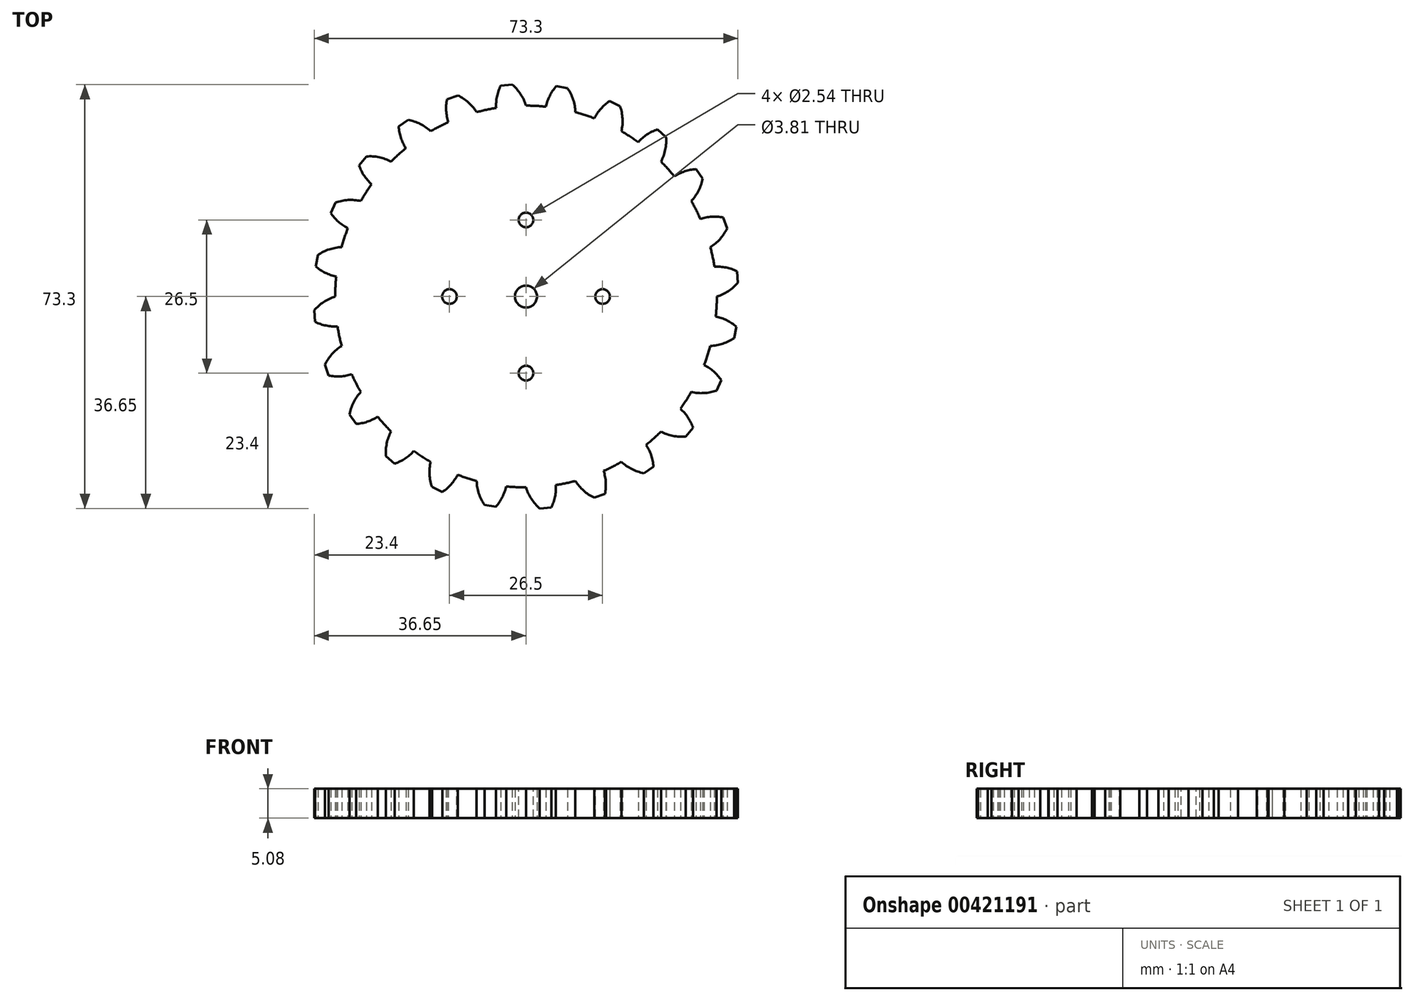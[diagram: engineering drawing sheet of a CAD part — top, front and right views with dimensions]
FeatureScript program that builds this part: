
annotation { "Feature Type Name" : "Feature", "Feature Type Description" : "" }
export const myFeature = defineFeature(function(context is Context, id is Id, definition is map)
    precondition{}
    {
        {
            var Q0;
            Q0=qCreatedBy(makeId("Top.planeOp"),FACE);
            var sketch = newSketch(context, id + "F0", { "sketchPlane" : qUnion([Q0])});
            skCircle(sketch, "E0", {"center": v(-444.5, 30.48) * mm, "radius": 1.9 * mm});
            skArc(sketch, "E1", {"start": v(-411.89, 35.65) * mm, "mid": v(-477.42, 27.89) * mm, "end": v(-411.48, 30.48) * mm});
            skArc(sketch, "E2", {"start": v(-408, 34.85) * mm, "mid": v(-409.9, 35.5) * mm, "end": v(-411.89, 35.65) * mm});
            skArc(sketch, "E3", {"start": v(-411.48, 30.48) * mm, "mid": v(-409.5, 31.41) * mm, "end": v(-407.85, 32.86) * mm});
            skLineSegment(sketch, "E4", {"start": v(-407.85, 32.86) * mm, "end": v(-408, 34.85) * mm});
            skSolve(sketch);
        }
        {
            var Q0;
            Q0=makeQuery(id+"F0.imprint","IMPRINT",FACE,{"disambiguationData":[TD([[makeQuery(id+"F0.imprint","IMPRINT",EDGE,{"derivedFrom":sQuery(id+"F0.wireOp",EDGE,"E0")}),-1.0]])]});
            extrude(context, id + "F1", {"entities" : qUnion([Q0]), "depth" : 5.08 * mm});
        }
        {
            var Q0;
            Q0=makeQuery(id+"F1.opExtrude","SWEPT_BODY",BODY,{"disambiguationData":[OSD([sQuery(id+"F0.wireOp",EDGE,"E0"),sQuery(id+"F0.wireOp",EDGE,"mfvC6Oh1-3P4Q-e3RM-1CXu-yx0pQRPToK0Y"),sQuery(id+"F0.wireOp",EDGE,"9eBLdcwT-yV5s-1o6b-eXcZ-bTUMROUA1rMA"),sQuery(id+"F0.wireOp",EDGE,"zkpdbw0p-lr3g-EBgj-NubB-pjmDa1DJFhjj"),sQuery(id+"F0.wireOp",EDGE,"jBF4Mbbw-OiBo-sLmE-1t8X-jgWY8rPl5u1C")])]});
            var Q1;
            Q1=makeQuery(id+"F1.opExtrude","SWEPT_FACE",FACE,{"disambiguationData":[OSD([sQuery(id+"F0.wireOp",EDGE,"E1")])]});
            circularPattern(context, id + "F2", {"entities" : qUnion([Q0]), "axis" : qUnion([Q1]), "angle" : 360 * degree, "instanceCount" : 24, "equalSpace" : true});
        }
        {
            var Q0;
            Q0=makeQuery(id+"F1.opExtrude","SWEPT_BODY",BODY,{"disambiguationData":[OSD([sQuery(id+"F0.wireOp",EDGE,"E0"),sQuery(id+"F0.wireOp",EDGE,"9eBLdcwT-yV5s-1o6b-eXcZ-bTUMROUA1rMA"),sQuery(id+"F0.wireOp",EDGE,"zkpdbw0p-lr3g-EBgj-NubB-pjmDa1DJFhjj"),sQuery(id+"F0.wireOp",EDGE,"jBF4Mbbw-OiBo-sLmE-1t8X-jgWY8rPl5u1C"),sQuery(id+"F0.wireOp",EDGE,"E1")])]});
            var Q1;
            Q1=makeQuery(id+"F2.opPattern","COPY",BODY,{"derivedFrom":makeQuery(id+"F1.opExtrude","SWEPT_BODY",BODY,{"disambiguationData":[OSD([sQuery(id+"F0.wireOp",EDGE,"E0"),sQuery(id+"F0.wireOp",EDGE,"9eBLdcwT-yV5s-1o6b-eXcZ-bTUMROUA1rMA"),sQuery(id+"F0.wireOp",EDGE,"zkpdbw0p-lr3g-EBgj-NubB-pjmDa1DJFhjj"),sQuery(id+"F0.wireOp",EDGE,"jBF4Mbbw-OiBo-sLmE-1t8X-jgWY8rPl5u1C"),sQuery(id+"F0.wireOp",EDGE,"E1")])]}),"instanceName":"1"});
            var Q2;
            Q2=makeQuery(id+"F2.opPattern","COPY",BODY,{"derivedFrom":makeQuery(id+"F1.opExtrude","SWEPT_BODY",BODY,{"disambiguationData":[OSD([sQuery(id+"F0.wireOp",EDGE,"E0"),sQuery(id+"F0.wireOp",EDGE,"9eBLdcwT-yV5s-1o6b-eXcZ-bTUMROUA1rMA"),sQuery(id+"F0.wireOp",EDGE,"zkpdbw0p-lr3g-EBgj-NubB-pjmDa1DJFhjj"),sQuery(id+"F0.wireOp",EDGE,"jBF4Mbbw-OiBo-sLmE-1t8X-jgWY8rPl5u1C"),sQuery(id+"F0.wireOp",EDGE,"E1")])]}),"instanceName":"2"});
            var Q3;
            Q3=makeQuery(id+"F2.opPattern","COPY",BODY,{"derivedFrom":makeQuery(id+"F1.opExtrude","SWEPT_BODY",BODY,{"disambiguationData":[OSD([sQuery(id+"F0.wireOp",EDGE,"E0"),sQuery(id+"F0.wireOp",EDGE,"9eBLdcwT-yV5s-1o6b-eXcZ-bTUMROUA1rMA"),sQuery(id+"F0.wireOp",EDGE,"zkpdbw0p-lr3g-EBgj-NubB-pjmDa1DJFhjj"),sQuery(id+"F0.wireOp",EDGE,"jBF4Mbbw-OiBo-sLmE-1t8X-jgWY8rPl5u1C"),sQuery(id+"F0.wireOp",EDGE,"E1")])]}),"instanceName":"3"});
            var Q4;
            Q4=makeQuery(id+"F2.opPattern","COPY",BODY,{"derivedFrom":makeQuery(id+"F1.opExtrude","SWEPT_BODY",BODY,{"disambiguationData":[OSD([sQuery(id+"F0.wireOp",EDGE,"E0"),sQuery(id+"F0.wireOp",EDGE,"9eBLdcwT-yV5s-1o6b-eXcZ-bTUMROUA1rMA"),sQuery(id+"F0.wireOp",EDGE,"zkpdbw0p-lr3g-EBgj-NubB-pjmDa1DJFhjj"),sQuery(id+"F0.wireOp",EDGE,"jBF4Mbbw-OiBo-sLmE-1t8X-jgWY8rPl5u1C"),sQuery(id+"F0.wireOp",EDGE,"E1")])]}),"instanceName":"4"});
            var Q5;
            Q5=makeQuery(id+"F2.opPattern","COPY",BODY,{"derivedFrom":makeQuery(id+"F1.opExtrude","SWEPT_BODY",BODY,{"disambiguationData":[OSD([sQuery(id+"F0.wireOp",EDGE,"E0"),sQuery(id+"F0.wireOp",EDGE,"9eBLdcwT-yV5s-1o6b-eXcZ-bTUMROUA1rMA"),sQuery(id+"F0.wireOp",EDGE,"zkpdbw0p-lr3g-EBgj-NubB-pjmDa1DJFhjj"),sQuery(id+"F0.wireOp",EDGE,"jBF4Mbbw-OiBo-sLmE-1t8X-jgWY8rPl5u1C"),sQuery(id+"F0.wireOp",EDGE,"E1")])]}),"instanceName":"5"});
            var Q6;
            Q6=makeQuery(id+"F2.opPattern","COPY",BODY,{"derivedFrom":makeQuery(id+"F1.opExtrude","SWEPT_BODY",BODY,{"disambiguationData":[OSD([sQuery(id+"F0.wireOp",EDGE,"E0"),sQuery(id+"F0.wireOp",EDGE,"9eBLdcwT-yV5s-1o6b-eXcZ-bTUMROUA1rMA"),sQuery(id+"F0.wireOp",EDGE,"zkpdbw0p-lr3g-EBgj-NubB-pjmDa1DJFhjj"),sQuery(id+"F0.wireOp",EDGE,"jBF4Mbbw-OiBo-sLmE-1t8X-jgWY8rPl5u1C"),sQuery(id+"F0.wireOp",EDGE,"E1")])]}),"instanceName":"6"});
            var Q7;
            Q7=makeQuery(id+"F2.opPattern","COPY",BODY,{"derivedFrom":makeQuery(id+"F1.opExtrude","SWEPT_BODY",BODY,{"disambiguationData":[OSD([sQuery(id+"F0.wireOp",EDGE,"E0"),sQuery(id+"F0.wireOp",EDGE,"9eBLdcwT-yV5s-1o6b-eXcZ-bTUMROUA1rMA"),sQuery(id+"F0.wireOp",EDGE,"zkpdbw0p-lr3g-EBgj-NubB-pjmDa1DJFhjj"),sQuery(id+"F0.wireOp",EDGE,"jBF4Mbbw-OiBo-sLmE-1t8X-jgWY8rPl5u1C"),sQuery(id+"F0.wireOp",EDGE,"E1")])]}),"instanceName":"11"});
            var Q8;
            Q8=makeQuery(id+"F2.opPattern","COPY",BODY,{"derivedFrom":makeQuery(id+"F1.opExtrude","SWEPT_BODY",BODY,{"disambiguationData":[OSD([sQuery(id+"F0.wireOp",EDGE,"E0"),sQuery(id+"F0.wireOp",EDGE,"9eBLdcwT-yV5s-1o6b-eXcZ-bTUMROUA1rMA"),sQuery(id+"F0.wireOp",EDGE,"zkpdbw0p-lr3g-EBgj-NubB-pjmDa1DJFhjj"),sQuery(id+"F0.wireOp",EDGE,"jBF4Mbbw-OiBo-sLmE-1t8X-jgWY8rPl5u1C"),sQuery(id+"F0.wireOp",EDGE,"E1")])]}),"instanceName":"14"});
            var Q9;
            Q9=makeQuery(id+"F2.opPattern","COPY",BODY,{"derivedFrom":makeQuery(id+"F1.opExtrude","SWEPT_BODY",BODY,{"disambiguationData":[OSD([sQuery(id+"F0.wireOp",EDGE,"E0"),sQuery(id+"F0.wireOp",EDGE,"9eBLdcwT-yV5s-1o6b-eXcZ-bTUMROUA1rMA"),sQuery(id+"F0.wireOp",EDGE,"zkpdbw0p-lr3g-EBgj-NubB-pjmDa1DJFhjj"),sQuery(id+"F0.wireOp",EDGE,"jBF4Mbbw-OiBo-sLmE-1t8X-jgWY8rPl5u1C"),sQuery(id+"F0.wireOp",EDGE,"E1")])]}),"instanceName":"12"});
            var Q10;
            Q10=makeQuery(id+"F2.opPattern","COPY",BODY,{"derivedFrom":makeQuery(id+"F1.opExtrude","SWEPT_BODY",BODY,{"disambiguationData":[OSD([sQuery(id+"F0.wireOp",EDGE,"E0"),sQuery(id+"F0.wireOp",EDGE,"9eBLdcwT-yV5s-1o6b-eXcZ-bTUMROUA1rMA"),sQuery(id+"F0.wireOp",EDGE,"zkpdbw0p-lr3g-EBgj-NubB-pjmDa1DJFhjj"),sQuery(id+"F0.wireOp",EDGE,"jBF4Mbbw-OiBo-sLmE-1t8X-jgWY8rPl5u1C"),sQuery(id+"F0.wireOp",EDGE,"E1")])]}),"instanceName":"13"});
            var Q11;
            Q11=makeQuery(id+"F2.opPattern","COPY",BODY,{"derivedFrom":makeQuery(id+"F1.opExtrude","SWEPT_BODY",BODY,{"disambiguationData":[OSD([sQuery(id+"F0.wireOp",EDGE,"E0"),sQuery(id+"F0.wireOp",EDGE,"9eBLdcwT-yV5s-1o6b-eXcZ-bTUMROUA1rMA"),sQuery(id+"F0.wireOp",EDGE,"zkpdbw0p-lr3g-EBgj-NubB-pjmDa1DJFhjj"),sQuery(id+"F0.wireOp",EDGE,"jBF4Mbbw-OiBo-sLmE-1t8X-jgWY8rPl5u1C"),sQuery(id+"F0.wireOp",EDGE,"E1")])]}),"instanceName":"19"});
            var Q12;
            Q12=makeQuery(id+"F2.opPattern","COPY",BODY,{"derivedFrom":makeQuery(id+"F1.opExtrude","SWEPT_BODY",BODY,{"disambiguationData":[OSD([sQuery(id+"F0.wireOp",EDGE,"E0"),sQuery(id+"F0.wireOp",EDGE,"9eBLdcwT-yV5s-1o6b-eXcZ-bTUMROUA1rMA"),sQuery(id+"F0.wireOp",EDGE,"zkpdbw0p-lr3g-EBgj-NubB-pjmDa1DJFhjj"),sQuery(id+"F0.wireOp",EDGE,"jBF4Mbbw-OiBo-sLmE-1t8X-jgWY8rPl5u1C"),sQuery(id+"F0.wireOp",EDGE,"E1")])]}),"instanceName":"18"});
            var Q13;
            Q13=makeQuery(id+"F2.opPattern","COPY",BODY,{"derivedFrom":makeQuery(id+"F1.opExtrude","SWEPT_BODY",BODY,{"disambiguationData":[OSD([sQuery(id+"F0.wireOp",EDGE,"E0"),sQuery(id+"F0.wireOp",EDGE,"9eBLdcwT-yV5s-1o6b-eXcZ-bTUMROUA1rMA"),sQuery(id+"F0.wireOp",EDGE,"zkpdbw0p-lr3g-EBgj-NubB-pjmDa1DJFhjj"),sQuery(id+"F0.wireOp",EDGE,"jBF4Mbbw-OiBo-sLmE-1t8X-jgWY8rPl5u1C"),sQuery(id+"F0.wireOp",EDGE,"E1")])]}),"instanceName":"17"});
            var Q14;
            Q14=makeQuery(id+"F2.opPattern","COPY",BODY,{"derivedFrom":makeQuery(id+"F1.opExtrude","SWEPT_BODY",BODY,{"disambiguationData":[OSD([sQuery(id+"F0.wireOp",EDGE,"E0"),sQuery(id+"F0.wireOp",EDGE,"9eBLdcwT-yV5s-1o6b-eXcZ-bTUMROUA1rMA"),sQuery(id+"F0.wireOp",EDGE,"zkpdbw0p-lr3g-EBgj-NubB-pjmDa1DJFhjj"),sQuery(id+"F0.wireOp",EDGE,"jBF4Mbbw-OiBo-sLmE-1t8X-jgWY8rPl5u1C"),sQuery(id+"F0.wireOp",EDGE,"E1")])]}),"instanceName":"10"});
            var Q15;
            Q15=makeQuery(id+"F2.opPattern","COPY",BODY,{"derivedFrom":makeQuery(id+"F1.opExtrude","SWEPT_BODY",BODY,{"disambiguationData":[OSD([sQuery(id+"F0.wireOp",EDGE,"E0"),sQuery(id+"F0.wireOp",EDGE,"9eBLdcwT-yV5s-1o6b-eXcZ-bTUMROUA1rMA"),sQuery(id+"F0.wireOp",EDGE,"zkpdbw0p-lr3g-EBgj-NubB-pjmDa1DJFhjj"),sQuery(id+"F0.wireOp",EDGE,"jBF4Mbbw-OiBo-sLmE-1t8X-jgWY8rPl5u1C"),sQuery(id+"F0.wireOp",EDGE,"E1")])]}),"instanceName":"16"});
            var Q16;
            Q16=makeQuery(id+"F2.opPattern","COPY",BODY,{"derivedFrom":makeQuery(id+"F1.opExtrude","SWEPT_BODY",BODY,{"disambiguationData":[OSD([sQuery(id+"F0.wireOp",EDGE,"E0"),sQuery(id+"F0.wireOp",EDGE,"9eBLdcwT-yV5s-1o6b-eXcZ-bTUMROUA1rMA"),sQuery(id+"F0.wireOp",EDGE,"zkpdbw0p-lr3g-EBgj-NubB-pjmDa1DJFhjj"),sQuery(id+"F0.wireOp",EDGE,"jBF4Mbbw-OiBo-sLmE-1t8X-jgWY8rPl5u1C"),sQuery(id+"F0.wireOp",EDGE,"E1")])]}),"instanceName":"15"});
            var Q17;
            Q17=makeQuery(id+"F2.opPattern","COPY",BODY,{"derivedFrom":makeQuery(id+"F1.opExtrude","SWEPT_BODY",BODY,{"disambiguationData":[OSD([sQuery(id+"F0.wireOp",EDGE,"E0"),sQuery(id+"F0.wireOp",EDGE,"9eBLdcwT-yV5s-1o6b-eXcZ-bTUMROUA1rMA"),sQuery(id+"F0.wireOp",EDGE,"zkpdbw0p-lr3g-EBgj-NubB-pjmDa1DJFhjj"),sQuery(id+"F0.wireOp",EDGE,"jBF4Mbbw-OiBo-sLmE-1t8X-jgWY8rPl5u1C"),sQuery(id+"F0.wireOp",EDGE,"E1")])]}),"instanceName":"9"});
            var Q18;
            Q18=makeQuery(id+"F2.opPattern","COPY",BODY,{"derivedFrom":makeQuery(id+"F1.opExtrude","SWEPT_BODY",BODY,{"disambiguationData":[OSD([sQuery(id+"F0.wireOp",EDGE,"E0"),sQuery(id+"F0.wireOp",EDGE,"9eBLdcwT-yV5s-1o6b-eXcZ-bTUMROUA1rMA"),sQuery(id+"F0.wireOp",EDGE,"zkpdbw0p-lr3g-EBgj-NubB-pjmDa1DJFhjj"),sQuery(id+"F0.wireOp",EDGE,"jBF4Mbbw-OiBo-sLmE-1t8X-jgWY8rPl5u1C"),sQuery(id+"F0.wireOp",EDGE,"E1")])]}),"instanceName":"8"});
            var Q19;
            Q19=makeQuery(id+"F2.opPattern","COPY",BODY,{"derivedFrom":makeQuery(id+"F1.opExtrude","SWEPT_BODY",BODY,{"disambiguationData":[OSD([sQuery(id+"F0.wireOp",EDGE,"E0"),sQuery(id+"F0.wireOp",EDGE,"9eBLdcwT-yV5s-1o6b-eXcZ-bTUMROUA1rMA"),sQuery(id+"F0.wireOp",EDGE,"zkpdbw0p-lr3g-EBgj-NubB-pjmDa1DJFhjj"),sQuery(id+"F0.wireOp",EDGE,"jBF4Mbbw-OiBo-sLmE-1t8X-jgWY8rPl5u1C"),sQuery(id+"F0.wireOp",EDGE,"E1")])]}),"instanceName":"7"});
            booleanBodies(context, id + "F3", {"operationType" : BooleanOperationType.UNION, "tools" : qUnion([Q0, Q1, Q2, Q3, Q4, Q5, Q6, Q7, Q8, Q9, Q10, Q11, Q12, Q13, Q14, Q15, Q16, Q17, Q18, Q19])});
        }
        {
            var Q0;
            Q0=makeQuery(id+"F2.opPattern","COPY",BODY,{"derivedFrom":makeQuery(id+"F1.opExtrude","SWEPT_BODY",BODY,{"disambiguationData":[OSD([sQuery(id+"F0.wireOp",EDGE,"E0"),sQuery(id+"F0.wireOp",EDGE,"E1"),sQuery(id+"F0.wireOp",EDGE,"E2"),sQuery(id+"F0.wireOp",EDGE,"E3"),sQuery(id+"F0.wireOp",EDGE,"E4")])]}),"instanceName":"20"});
            var Q1;
            Q1=makeQuery(id+"F1.opExtrude","SWEPT_BODY",BODY,{"disambiguationData":[OSD([sQuery(id+"F0.wireOp",EDGE,"E0"),sQuery(id+"F0.wireOp",EDGE,"E1"),sQuery(id+"F0.wireOp",EDGE,"E2"),sQuery(id+"F0.wireOp",EDGE,"E3"),sQuery(id+"F0.wireOp",EDGE,"E4")])]});
            var Q2;
            Q2=makeQuery(id+"F2.opPattern","COPY",BODY,{"derivedFrom":makeQuery(id+"F1.opExtrude","SWEPT_BODY",BODY,{"disambiguationData":[OSD([sQuery(id+"F0.wireOp",EDGE,"E0"),sQuery(id+"F0.wireOp",EDGE,"E1"),sQuery(id+"F0.wireOp",EDGE,"E2"),sQuery(id+"F0.wireOp",EDGE,"E3"),sQuery(id+"F0.wireOp",EDGE,"E4")])]}),"instanceName":"21"});
            var Q3;
            Q3=makeQuery(id+"F2.opPattern","COPY",BODY,{"derivedFrom":makeQuery(id+"F1.opExtrude","SWEPT_BODY",BODY,{"disambiguationData":[OSD([sQuery(id+"F0.wireOp",EDGE,"E0"),sQuery(id+"F0.wireOp",EDGE,"E1"),sQuery(id+"F0.wireOp",EDGE,"E2"),sQuery(id+"F0.wireOp",EDGE,"E3"),sQuery(id+"F0.wireOp",EDGE,"E4")])]}),"instanceName":"22"});
            var Q4;
            Q4=makeQuery(id+"F2.opPattern","COPY",BODY,{"derivedFrom":makeQuery(id+"F1.opExtrude","SWEPT_BODY",BODY,{"disambiguationData":[OSD([sQuery(id+"F0.wireOp",EDGE,"E0"),sQuery(id+"F0.wireOp",EDGE,"E1"),sQuery(id+"F0.wireOp",EDGE,"E2"),sQuery(id+"F0.wireOp",EDGE,"E3"),sQuery(id+"F0.wireOp",EDGE,"E4")])]}),"instanceName":"23"});
            booleanBodies(context, id + "F4", {"operationType" : BooleanOperationType.UNION, "tools" : qUnion([Q0, Q1, Q2, Q3, Q4])});
        }
        {
            var Q0;
            {var subQ0=makeQuery(id+"F1.opExtrude","CAP_FACE",FACE,{"disambiguationData":[OSD([sQuery(id+"F0.wireOp",EDGE,"E0"),sQuery(id+"F0.wireOp",EDGE,"E1"),sQuery(id+"F0.wireOp",EDGE,"E2"),sQuery(id+"F0.wireOp",EDGE,"E3"),sQuery(id+"F0.wireOp",EDGE,"E4")])],"isStart":false});Q0=makeQuery(id+"F4.opBoolean","MERGE",FACE,{"derivedFrom":[makeQuery(id+"F2.opPattern","COPY",FACE,{"derivedFrom":subQ0,"instanceName":"20"}),makeQuery(id+"F2.opPattern","COPY",FACE,{"derivedFrom":subQ0,"instanceName":"21"}),makeQuery(id+"F2.opPattern","COPY",FACE,{"derivedFrom":subQ0,"instanceName":"22"}),makeQuery(id+"F2.opPattern","COPY",FACE,{"derivedFrom":subQ0,"instanceName":"23"}),makeQuery(id+"F3.opBoolean","MERGE",FACE,{"derivedFrom":[subQ0,makeQuery(id+"F2.opPattern","COPY",FACE,{"derivedFrom":subQ0,"instanceName":"1"}),makeQuery(id+"F2.opPattern","COPY",FACE,{"derivedFrom":subQ0,"instanceName":"2"}),makeQuery(id+"F2.opPattern","COPY",FACE,{"derivedFrom":subQ0,"instanceName":"3"}),makeQuery(id+"F2.opPattern","COPY",FACE,{"derivedFrom":subQ0,"instanceName":"4"}),makeQuery(id+"F2.opPattern","COPY",FACE,{"derivedFrom":subQ0,"instanceName":"5"}),makeQuery(id+"F2.opPattern","COPY",FACE,{"derivedFrom":subQ0,"instanceName":"6"}),makeQuery(id+"F2.opPattern","COPY",FACE,{"derivedFrom":subQ0,"instanceName":"7"}),makeQuery(id+"F2.opPattern","COPY",FACE,{"derivedFrom":subQ0,"instanceName":"8"}),makeQuery(id+"F2.opPattern","COPY",FACE,{"derivedFrom":subQ0,"instanceName":"9"}),makeQuery(id+"F2.opPattern","COPY",FACE,{"derivedFrom":subQ0,"instanceName":"10"}),makeQuery(id+"F2.opPattern","COPY",FACE,{"derivedFrom":subQ0,"instanceName":"11"}),makeQuery(id+"F2.opPattern","COPY",FACE,{"derivedFrom":subQ0,"instanceName":"12"}),makeQuery(id+"F2.opPattern","COPY",FACE,{"derivedFrom":subQ0,"instanceName":"13"}),makeQuery(id+"F2.opPattern","COPY",FACE,{"derivedFrom":subQ0,"instanceName":"14"}),makeQuery(id+"F2.opPattern","COPY",FACE,{"derivedFrom":subQ0,"instanceName":"15"}),makeQuery(id+"F2.opPattern","COPY",FACE,{"derivedFrom":subQ0,"instanceName":"16"}),makeQuery(id+"F2.opPattern","COPY",FACE,{"derivedFrom":subQ0,"instanceName":"17"}),makeQuery(id+"F2.opPattern","COPY",FACE,{"derivedFrom":subQ0,"instanceName":"18"}),makeQuery(id+"F2.opPattern","COPY",FACE,{"derivedFrom":subQ0,"instanceName":"19"})]})]});}
            var sketch = newSketch(context, id + "F5", { "sketchPlane" : qUnion([Q0])});
            skLineSegment(sketch, "E5", {"start": v(-444.5, 30.48) * mm, "end": v(-444.5, 43.73) * mm});
            skCircle(sketch, "E6", {"center": v(-444.5, 43.73) * mm, "radius": 1.27 * mm});
            skCircle(sketch, "E7.1.0", {"center": v(-457.75, 30.48) * mm, "radius": 1.27 * mm});
            skCircle(sketch, "E7.2.0", {"center": v(-444.5, 17.23) * mm, "radius": 1.27 * mm});
            skCircle(sketch, "E7.3.0", {"center": v(-431.25, 30.48) * mm, "radius": 1.27 * mm});
            skPoint(sketch, "E7.center", {"position": v(-444.5, 30.48) * mm});
            skSolve(sketch);
        }
        {
            var Q0;
            Q0=makeQuery(id+"F5.imprint","IMPRINT",FACE,{"disambiguationData":[TD([[makeQuery(id+"F5.imprint","IMPRINT",EDGE,{"derivedFrom":sQuery(id+"F5.wireOp",EDGE,"E6")}),1.0]])]});
            var Q1;
            Q1=makeQuery(id+"F5.imprint","IMPRINT",FACE,{"disambiguationData":[TD([[makeQuery(id+"F5.imprint","IMPRINT",EDGE,{"derivedFrom":sQuery(id+"F5.wireOp",EDGE,"E7.3.0")}),1.0]])]});
            var Q2;
            Q2=makeQuery(id+"F5.imprint","IMPRINT",FACE,{"disambiguationData":[TD([[makeQuery(id+"F5.imprint","IMPRINT",EDGE,{"derivedFrom":sQuery(id+"F5.wireOp",EDGE,"E7.2.0")}),1.0]])]});
            var Q3;
            Q3=makeQuery(id+"F5.imprint","IMPRINT",FACE,{"disambiguationData":[TD([[makeQuery(id+"F5.imprint","IMPRINT",EDGE,{"derivedFrom":sQuery(id+"F5.wireOp",EDGE,"E7.1.0")}),1.0]])]});
            extrude(context, id + "F6", {"entities" : qUnion([Q0, Q1, Q2, Q3]), "operationType" : NewBodyOperationType.REMOVE, "oppositeDirection" : true, "depth" : 25.4 * mm});
        }
    });
